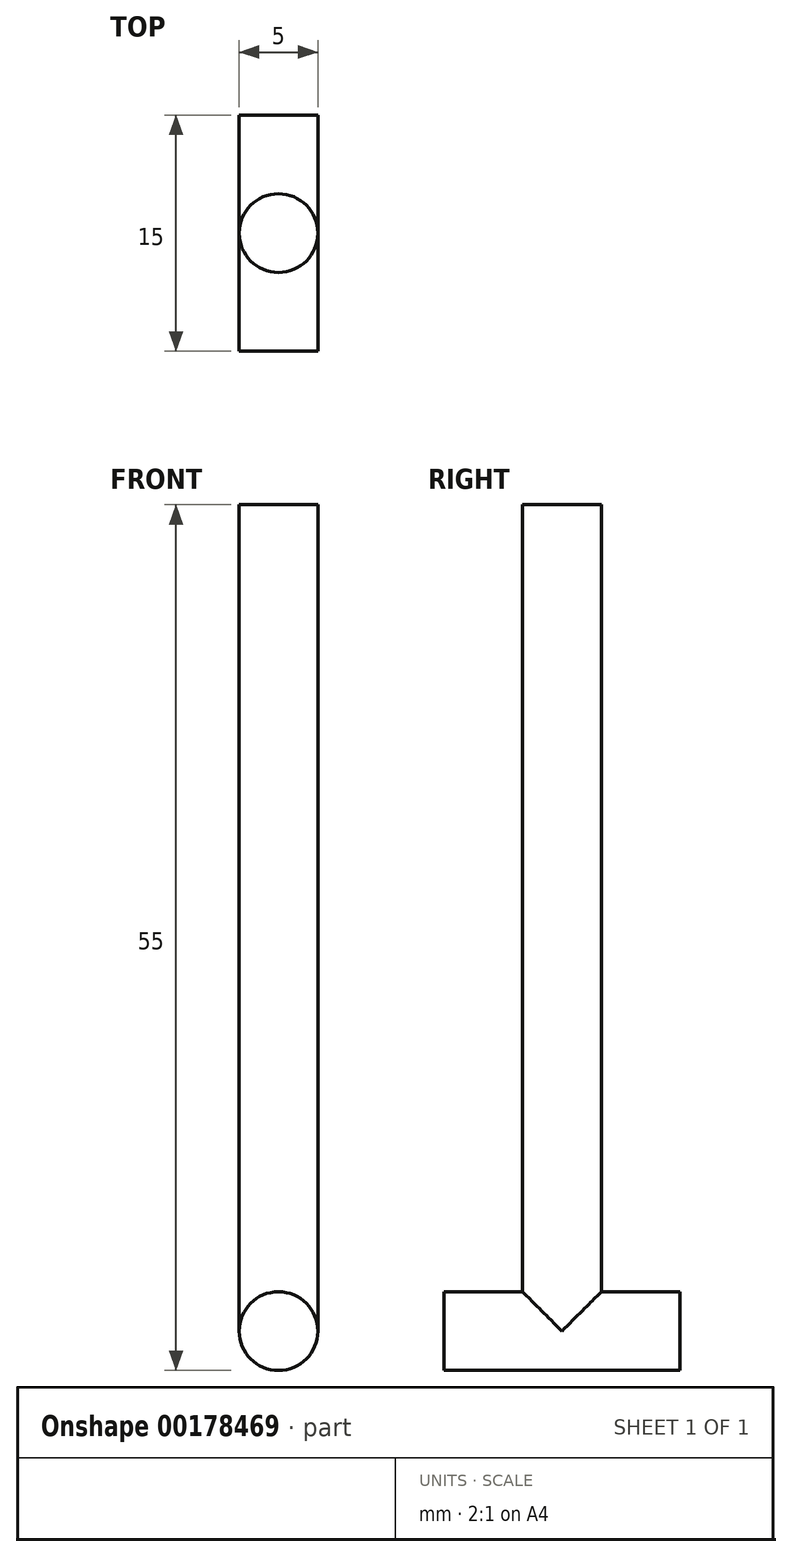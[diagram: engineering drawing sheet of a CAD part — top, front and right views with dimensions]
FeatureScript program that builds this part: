
annotation { "Feature Type Name" : "Feature", "Feature Type Description" : "" }
export const myFeature = defineFeature(function(context is Context, id is Id, definition is map)
    precondition{}
    {
        {
            var Q0;
            Q0=qCreatedBy(makeId("Top.planeOp"),FACE);
            var sketch = newSketch(context, id + "F0", { "sketchPlane" : qUnion([Q0])});
            skLineSegment(sketch, "E0.bottom", {"start": v(-37.27, -29.83) * mm, "end": v(-32.27, -29.83) * mm});
            skLineSegment(sketch, "E0.top", {"start": v(-37.27, -14.83) * mm, "end": v(-32.27, -14.83) * mm});
            skLineSegment(sketch, "E0.left", {"start": v(-37.27, -29.83) * mm, "end": v(-37.27, -14.83) * mm});
            skLineSegment(sketch, "E0.right", {"start": v(-32.27, -29.83) * mm, "end": v(-32.27, -14.83) * mm});
            skSolve(sketch);
        }
        {
            var Q0;
            Q0=makeQuery(id+"F0.imprint","IMPRINT",FACE,{"disambiguationData":[TD([[makeQuery(id+"F0.imprint","IMPRINT",EDGE,{"derivedFrom":sQuery(id+"F0.wireOp",EDGE,"E0.bottom")}),1.0]])]});
            extrude(context, id + "F1", {"entities" : qUnion([Q0]), "depth" : 5 * mm});
        }
        {
            var Q0;
            Q0=makeQuery(id+"F1.opExtrude","CAP_FACE",FACE,{"disambiguationData":[OSD([sQuery(id+"F0.wireOp",EDGE,"E0.bottom"),sQuery(id+"F0.wireOp",EDGE,"E0.top"),sQuery(id+"F0.wireOp",EDGE,"E0.left"),sQuery(id+"F0.wireOp",EDGE,"E0.right")])],"isStart":false});
            var sketch = newSketch(context, id + "F2", { "sketchPlane" : qUnion([Q0])});
            skLineSegment(sketch, "E1", {"start": v(-37.27, -14.83) * mm, "end": v(-32.27, -29.83) * mm, "construction": true});
            skLineSegment(sketch, "E2", {"start": v(-32.27, -29.83) * mm, "end": v(-37.27, -29.83) * mm, "construction": true});
            skLineSegment(sketch, "E3", {"start": v(-37.27, -29.83) * mm, "end": v(-32.27, -14.83) * mm, "construction": true});
            skCircle(sketch, "E4", {"center": v(-34.77, -22.33) * mm, "radius": 2.5 * mm});
            skSolve(sketch);
        }
        {
            var Q0;
            {var subQ0=sQuery(id+"F2.wireOp",EDGE,"E4");var subQ1=makeQuery(id+"F2.imprint","INTERSECT",VERTEX,{"derivedFrom":[makeQuery(id+"F1.opExtrude","CAP_EDGE",EDGE,{"disambiguationData":[OSD([sQuery(id+"F0.wireOp",EDGE,"E0.left")])],"isStart":false}),subQ0]});Q0=makeQuery(id+"F2.imprint","IMPRINT",FACE,{"disambiguationData":[TD([[makeQuery(id+"F2.imprint","IMPRINT",EDGE,{"disambiguationData":[TD([[subQ1,1.0]])],"derivedFrom":subQ0}),1.0]])]});}
            extrude(context, id + "F3", {"entities" : qUnion([Q0]), "operationType" : NewBodyOperationType.ADD, "depth" : 25 * mm});
        }
        {
            var Q0;
            Q0=makeQuery(id+"F1.opExtrude","CAP_EDGE",EDGE,{"disambiguationData":[OSD([sQuery(id+"F0.wireOp",EDGE,"E0.left")])],"isStart":true});
            var Q1;
            Q1=makeQuery(id+"F1.opExtrude","CAP_EDGE",EDGE,{"disambiguationData":[OSD([sQuery(id+"F0.wireOp",EDGE,"E0.right")])],"isStart":true});
            var Q2;
            {var subQ0=sQuery(id+"F0.wireOp",EDGE,"E0.bottom");var subQ1=sQuery(id+"F0.wireOp",EDGE,"E0.right");Q2=makeQuery(id+"F3.boolean.opBoolean","SPLIT",EDGE,{"disambiguationData":[TD([makeQuery(id+"F1.opExtrude","SWEPT_FACE",FACE,{"disambiguationData":[OSD([subQ0])]})])],"derivedFrom":makeQuery(id+"F1.opExtrude","CAP_EDGE",EDGE,{"disambiguationData":[OSD([subQ1])],"isStart":false})});}
            var Q3;
            {var subQ0=sQuery(id+"F0.wireOp",EDGE,"E0.bottom");var subQ1=sQuery(id+"F0.wireOp",EDGE,"E0.left");Q3=makeQuery(id+"F3.boolean.opBoolean","SPLIT",EDGE,{"disambiguationData":[TD([makeQuery(id+"F1.opExtrude","SWEPT_FACE",FACE,{"disambiguationData":[OSD([subQ0])]})])],"derivedFrom":makeQuery(id+"F1.opExtrude","CAP_EDGE",EDGE,{"disambiguationData":[OSD([subQ1])],"isStart":false})});}
            fillet(context, id + "F4", {"entities" : qUnion([Q0, Q1, Q2, Q3]), "radius" : 2.5 * mm, "tangentPropagation" : true, "allowEdgeOverflow" : false});
        }
        {
            var Q0;
            Q0=makeQuery(id+"F3.opExtrude","CAP_FACE",FACE,{"disambiguationData":[OSD([sQuery(id+"F2.wireOp",EDGE,"E4")])],"isStart":false});
            extrude(context, id + "F5", {"entities" : qUnion([Q0]), "operationType" : NewBodyOperationType.ADD, "depth" : 25 * mm});
        }
    });
